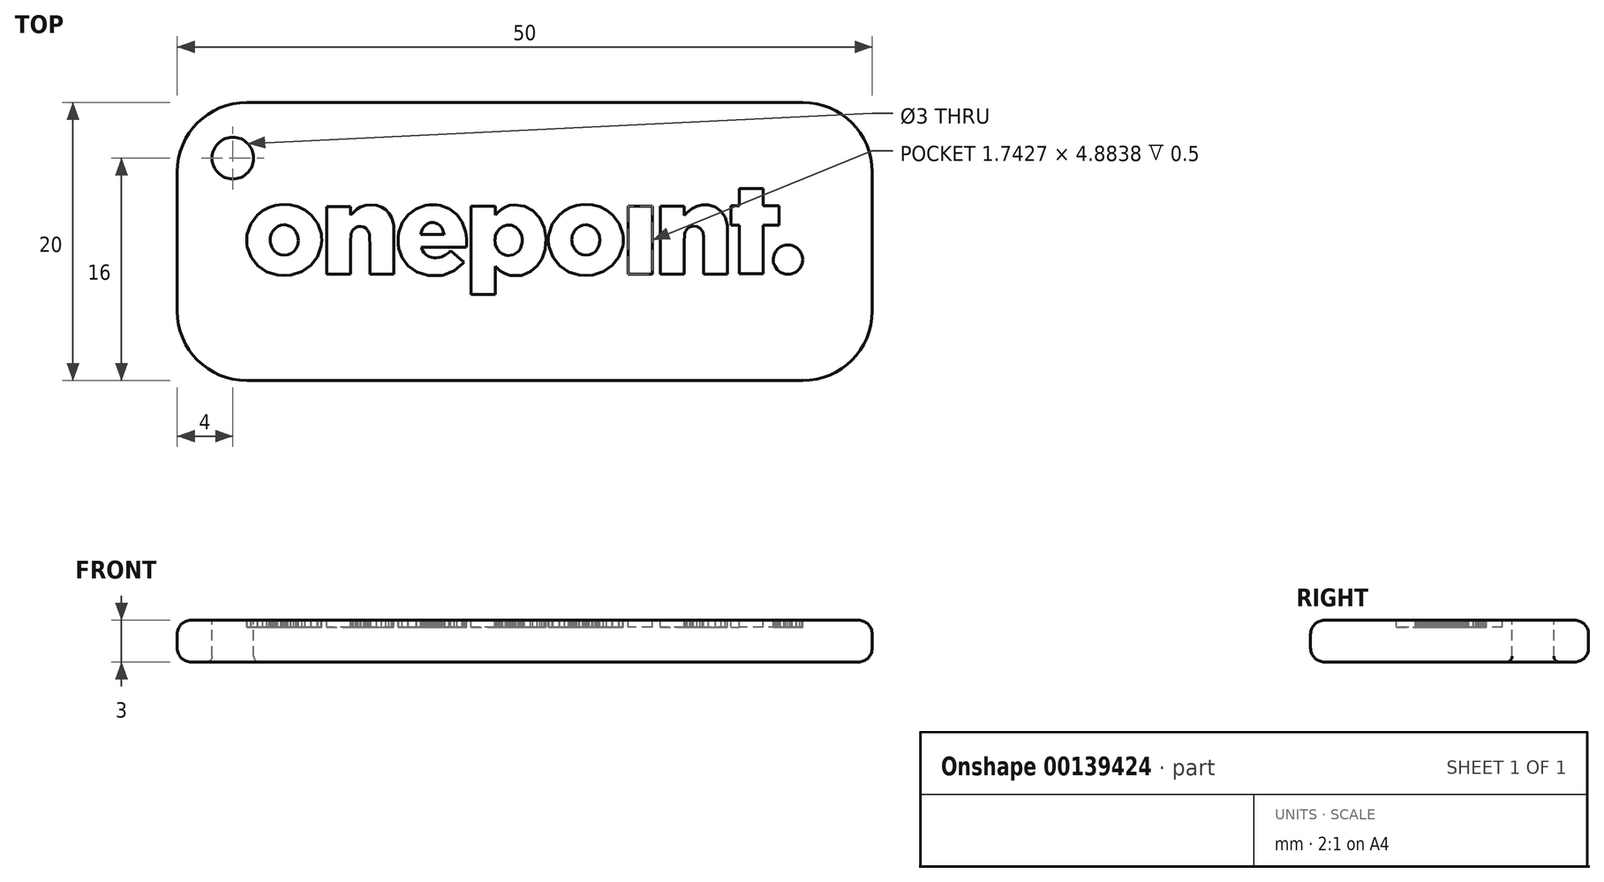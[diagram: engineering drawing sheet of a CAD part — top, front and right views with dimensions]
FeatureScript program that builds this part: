
annotation { "Feature Type Name" : "Feature", "Feature Type Description" : "" }
export const myFeature = defineFeature(function(context is Context, id is Id, definition is map)
    precondition{}
    {
        {
            var Q0;
            Q0=qCreatedBy(makeId("Top.planeOp"),FACE);
            var sketch = newSketch(context, id + "F0", { "sketchPlane" : qUnion([Q0])});
            skLineSegment(sketch, "E0.bottom", {"start": v(-25, 10) * mm, "end": v(25, 10) * mm});
            skLineSegment(sketch, "E0.top", {"start": v(-25, -10) * mm, "end": v(25, -10) * mm});
            skLineSegment(sketch, "E0.left", {"start": v(-25, 10) * mm, "end": v(-25, -10) * mm});
            skLineSegment(sketch, "E0.right", {"start": v(25, 10) * mm, "end": v(25, -10) * mm});
            skSolve(sketch);
        }
        {
            var Q0;
            Q0=qCreatedBy(makeId("Top.planeOp"),FACE);
            var sketch = newSketch(context, id + "F1", { "sketchPlane" : qUnion([Q0])});
            skLineSegment(sketch, "E1", {"start": v(-17.78, -2.42) * mm, "end": v(-18.55, -2.18) * mm});
            skLineSegment(sketch, "E2", {"start": v(-18.55, -2.18) * mm, "end": v(-19.2, -1.75) * mm});
            skLineSegment(sketch, "E3", {"start": v(-19.2, -1.75) * mm, "end": v(-19.67, -1.15) * mm});
            skLineSegment(sketch, "E4", {"start": v(-19.67, -1.15) * mm, "end": v(-19.95, -0.41) * mm});
            skLineSegment(sketch, "E5", {"start": v(-19.95, -0.41) * mm, "end": v(-19.99, -0.22) * mm});
            skLineSegment(sketch, "E6", {"start": v(-19.99, -0.22) * mm, "end": v(-20, 0.02) * mm});
            skLineSegment(sketch, "E7", {"start": v(-20, 0.02) * mm, "end": v(-20, 0.27) * mm});
            skLineSegment(sketch, "E8", {"start": v(-20, 0.27) * mm, "end": v(-19.98, 0.48) * mm});
            skLineSegment(sketch, "E9", {"start": v(-19.98, 0.48) * mm, "end": v(-19.72, 1.26) * mm});
            skLineSegment(sketch, "E10", {"start": v(-19.72, 1.26) * mm, "end": v(-19.22, 1.91) * mm});
            skLineSegment(sketch, "E11", {"start": v(-19.22, 1.91) * mm, "end": v(-18.84, 2.22) * mm});
            skLineSegment(sketch, "E12", {"start": v(-18.84, 2.22) * mm, "end": v(-18.41, 2.45) * mm});
            skLineSegment(sketch, "E13", {"start": v(-18.41, 2.45) * mm, "end": v(-17.94, 2.6) * mm});
            skLineSegment(sketch, "E14", {"start": v(-17.94, 2.6) * mm, "end": v(-17.43, 2.66) * mm});
            skLineSegment(sketch, "E15", {"start": v(-17.43, 2.66) * mm, "end": v(-16.85, 2.63) * mm});
            skLineSegment(sketch, "E16", {"start": v(-16.85, 2.63) * mm, "end": v(-16.3, 2.5) * mm});
            skLineSegment(sketch, "E17", {"start": v(-16.3, 2.5) * mm, "end": v(-15.8, 2.25) * mm});
            skLineSegment(sketch, "E18", {"start": v(-15.8, 2.25) * mm, "end": v(-15.37, 1.91) * mm});
            skLineSegment(sketch, "E19", {"start": v(-15.37, 1.91) * mm, "end": v(-14.89, 1.28) * mm});
            skLineSegment(sketch, "E20", {"start": v(-14.89, 1.28) * mm, "end": v(-14.63, 0.55) * mm});
            skLineSegment(sketch, "E21", {"start": v(-14.63, 0.55) * mm, "end": v(-14.61, 0.34) * mm});
            skLineSegment(sketch, "E22", {"start": v(-14.61, 0.34) * mm, "end": v(-14.6, 0.1) * mm});
            skLineSegment(sketch, "E23", {"start": v(-14.6, 0.1) * mm, "end": v(-14.62, -0.15) * mm});
            skLineSegment(sketch, "E24", {"start": v(-14.62, -0.15) * mm, "end": v(-14.65, -0.36) * mm});
            skLineSegment(sketch, "E25", {"start": v(-14.65, -0.36) * mm, "end": v(-14.92, -1.1) * mm});
            skLineSegment(sketch, "E26", {"start": v(-14.92, -1.1) * mm, "end": v(-15.39, -1.71) * mm});
            skLineSegment(sketch, "E27", {"start": v(-15.39, -1.71) * mm, "end": v(-16.03, -2.16) * mm});
            skLineSegment(sketch, "E28", {"start": v(-16.03, -2.16) * mm, "end": v(-16.8, -2.4) * mm});
            skLineSegment(sketch, "E29", {"start": v(-16.8, -2.4) * mm, "end": v(-17.3, -2.44) * mm});
            skLineSegment(sketch, "E30", {"start": v(-17.3, -2.44) * mm, "end": v(-17.78, -2.42) * mm});
            skLineSegment(sketch, "E31", {"start": v(-17.78, -2.42) * mm, "end": v(-17.78, -2.42) * mm});
            skLineSegment(sketch, "E32", {"start": v(-17.04, -0.95) * mm, "end": v(-16.81, -0.86) * mm});
            skLineSegment(sketch, "E33", {"start": v(-16.81, -0.86) * mm, "end": v(-16.62, -0.72) * mm});
            skLineSegment(sketch, "E34", {"start": v(-16.62, -0.72) * mm, "end": v(-16.47, -0.53) * mm});
            skLineSegment(sketch, "E35", {"start": v(-16.47, -0.53) * mm, "end": v(-16.35, -0.29) * mm});
            skLineSegment(sketch, "E36", {"start": v(-16.35, -0.29) * mm, "end": v(-16.3, 0.07) * mm});
            skLineSegment(sketch, "E37", {"start": v(-16.3, 0.07) * mm, "end": v(-16.33, 0.42) * mm});
            skLineSegment(sketch, "E38", {"start": v(-16.33, 0.42) * mm, "end": v(-16.46, 0.7) * mm});
            skLineSegment(sketch, "E39", {"start": v(-16.46, 0.7) * mm, "end": v(-16.63, 0.91) * mm});
            skLineSegment(sketch, "E40", {"start": v(-16.63, 0.91) * mm, "end": v(-16.86, 1.07) * mm});
            skLineSegment(sketch, "E41", {"start": v(-16.86, 1.07) * mm, "end": v(-17.12, 1.17) * mm});
            skLineSegment(sketch, "E42", {"start": v(-17.12, 1.17) * mm, "end": v(-17.23, 1.2) * mm});
            skLineSegment(sketch, "E43", {"start": v(-17.23, 1.2) * mm, "end": v(-17.32, 1.2) * mm});
            skLineSegment(sketch, "E44", {"start": v(-17.32, 1.2) * mm, "end": v(-17.54, 1.17) * mm});
            skLineSegment(sketch, "E45", {"start": v(-17.54, 1.17) * mm, "end": v(-17.76, 1.09) * mm});
            skLineSegment(sketch, "E46", {"start": v(-17.76, 1.09) * mm, "end": v(-17.94, 0.97) * mm});
            skLineSegment(sketch, "E47", {"start": v(-17.94, 0.97) * mm, "end": v(-18.1, 0.8) * mm});
            skLineSegment(sketch, "E48", {"start": v(-18.1, 0.8) * mm, "end": v(-18.2, 0.62) * mm});
            skLineSegment(sketch, "E49", {"start": v(-18.2, 0.62) * mm, "end": v(-18.28, 0.41) * mm});
            skLineSegment(sketch, "E50", {"start": v(-18.28, 0.41) * mm, "end": v(-18.3, 0.27) * mm});
            skLineSegment(sketch, "E51", {"start": v(-18.3, 0.27) * mm, "end": v(-18.32, 0.11) * mm});
            skLineSegment(sketch, "E52", {"start": v(-18.32, 0.11) * mm, "end": v(-18.3, -0.05) * mm});
            skLineSegment(sketch, "E53", {"start": v(-18.3, -0.05) * mm, "end": v(-18.28, -0.17) * mm});
            skLineSegment(sketch, "E54", {"start": v(-18.28, -0.17) * mm, "end": v(-18.18, -0.44) * mm});
            skLineSegment(sketch, "E55", {"start": v(-18.18, -0.44) * mm, "end": v(-18.01, -0.67) * mm});
            skLineSegment(sketch, "E56", {"start": v(-18.01, -0.67) * mm, "end": v(-17.8, -0.84) * mm});
            skLineSegment(sketch, "E57", {"start": v(-17.8, -0.84) * mm, "end": v(-17.55, -0.95) * mm});
            skLineSegment(sketch, "E58", {"start": v(-17.55, -0.95) * mm, "end": v(-17.3, -0.98) * mm});
            skLineSegment(sketch, "E59", {"start": v(-17.3, -0.98) * mm, "end": v(-17.04, -0.95) * mm});
            skLineSegment(sketch, "E60", {"start": v(-17.04, -0.95) * mm, "end": v(-17.04, -0.95) * mm});
            skLineSegment(sketch, "E61", {"start": v(-14.26, 0.08) * mm, "end": v(-14.26, 2.52) * mm});
            skLineSegment(sketch, "E62", {"start": v(-14.26, 2.52) * mm, "end": v(-12.53, 2.52) * mm});
            skLineSegment(sketch, "E63", {"start": v(-12.53, 2.52) * mm, "end": v(-12.53, 1.9) * mm});
            skLineSegment(sketch, "E64", {"start": v(-12.53, 1.9) * mm, "end": v(-12.34, 2.07) * mm});
            skLineSegment(sketch, "E65", {"start": v(-12.34, 2.07) * mm, "end": v(-12.09, 2.3) * mm});
            skLineSegment(sketch, "E66", {"start": v(-12.09, 2.3) * mm, "end": v(-11.81, 2.46) * mm});
            skLineSegment(sketch, "E67", {"start": v(-11.81, 2.46) * mm, "end": v(-11.46, 2.6) * mm});
            skLineSegment(sketch, "E68", {"start": v(-11.46, 2.6) * mm, "end": v(-11.07, 2.64) * mm});
            skLineSegment(sketch, "E69", {"start": v(-11.07, 2.64) * mm, "end": v(-10.67, 2.6) * mm});
            skLineSegment(sketch, "E70", {"start": v(-10.67, 2.6) * mm, "end": v(-10.3, 2.48) * mm});
            skLineSegment(sketch, "E71", {"start": v(-10.3, 2.48) * mm, "end": v(-10, 2.28) * mm});
            skLineSegment(sketch, "E72", {"start": v(-10, 2.28) * mm, "end": v(-9.75, 2.03) * mm});
            skLineSegment(sketch, "E73", {"start": v(-9.75, 2.03) * mm, "end": v(-9.57, 1.7) * mm});
            skLineSegment(sketch, "E74", {"start": v(-9.57, 1.7) * mm, "end": v(-9.45, 1.3) * mm});
            skLineSegment(sketch, "E75", {"start": v(-9.45, 1.3) * mm, "end": v(-9.44, 1.25) * mm});
            skLineSegment(sketch, "E76", {"start": v(-9.44, 1.25) * mm, "end": v(-9.43, 1.17) * mm});
            skLineSegment(sketch, "E77", {"start": v(-9.43, 1.17) * mm, "end": v(-9.43, 1.06) * mm});
            skLineSegment(sketch, "E78", {"start": v(-9.43, 1.06) * mm, "end": v(-9.42, 0.89) * mm});
            skLineSegment(sketch, "E79", {"start": v(-9.42, 0.89) * mm, "end": v(-9.42, 0.65) * mm});
            skLineSegment(sketch, "E80", {"start": v(-9.42, 0.65) * mm, "end": v(-9.41, 0.34) * mm});
            skLineSegment(sketch, "E81", {"start": v(-9.41, 0.34) * mm, "end": v(-9.41, -0.08) * mm});
            skLineSegment(sketch, "E82", {"start": v(-9.41, -0.08) * mm, "end": v(-9.4, -0.6) * mm});
            skLineSegment(sketch, "E83", {"start": v(-9.4, -0.6) * mm, "end": v(-9.4, -2.36) * mm});
            skLineSegment(sketch, "E84", {"start": v(-9.4, -2.36) * mm, "end": v(-11.14, -2.36) * mm});
            skLineSegment(sketch, "E85", {"start": v(-11.14, -2.36) * mm, "end": v(-11.14, -0.94) * mm});
            skLineSegment(sketch, "E86", {"start": v(-11.14, -0.94) * mm, "end": v(-11.14, -0.47) * mm});
            skLineSegment(sketch, "E87", {"start": v(-11.14, -0.47) * mm, "end": v(-11.15, -0.12) * mm});
            skLineSegment(sketch, "E88", {"start": v(-11.15, -0.12) * mm, "end": v(-11.15, 0.14) * mm});
            skLineSegment(sketch, "E89", {"start": v(-11.15, 0.14) * mm, "end": v(-11.15, 0.32) * mm});
            skLineSegment(sketch, "E90", {"start": v(-11.15, 0.32) * mm, "end": v(-11.16, 0.44) * mm});
            skLineSegment(sketch, "E91", {"start": v(-11.16, 0.44) * mm, "end": v(-11.16, 0.52) * mm});
            skLineSegment(sketch, "E92", {"start": v(-11.16, 0.52) * mm, "end": v(-11.17, 0.57) * mm});
            skLineSegment(sketch, "E93", {"start": v(-11.17, 0.57) * mm, "end": v(-11.19, 0.6) * mm});
            skLineSegment(sketch, "E94", {"start": v(-11.19, 0.6) * mm, "end": v(-11.28, 0.8) * mm});
            skLineSegment(sketch, "E95", {"start": v(-11.28, 0.8) * mm, "end": v(-11.4, 0.95) * mm});
            skLineSegment(sketch, "E96", {"start": v(-11.4, 0.95) * mm, "end": v(-11.56, 1.05) * mm});
            skLineSegment(sketch, "E97", {"start": v(-11.56, 1.05) * mm, "end": v(-11.76, 1.09) * mm});
            skLineSegment(sketch, "E98", {"start": v(-11.76, 1.09) * mm, "end": v(-11.99, 1.08) * mm});
            skLineSegment(sketch, "E99", {"start": v(-11.99, 1.08) * mm, "end": v(-12.2, 0.99) * mm});
            skLineSegment(sketch, "E100", {"start": v(-12.2, 0.99) * mm, "end": v(-12.36, 0.84) * mm});
            skLineSegment(sketch, "E101", {"start": v(-12.36, 0.84) * mm, "end": v(-12.48, 0.63) * mm});
            skLineSegment(sketch, "E102", {"start": v(-12.48, 0.63) * mm, "end": v(-12.5, 0.6) * mm});
            skLineSegment(sketch, "E103", {"start": v(-12.5, 0.6) * mm, "end": v(-12.5, 0.55) * mm});
            skLineSegment(sketch, "E104", {"start": v(-12.5, 0.55) * mm, "end": v(-12.5, 0.47) * mm});
            skLineSegment(sketch, "E105", {"start": v(-12.5, 0.47) * mm, "end": v(-12.51, 0.35) * mm});
            skLineSegment(sketch, "E106", {"start": v(-12.51, 0.35) * mm, "end": v(-12.52, 0.17) * mm});
            skLineSegment(sketch, "E107", {"start": v(-12.52, 0.17) * mm, "end": v(-12.52, -0.1) * mm});
            skLineSegment(sketch, "E108", {"start": v(-12.52, -0.1) * mm, "end": v(-12.52, -0.45) * mm});
            skLineSegment(sketch, "E109", {"start": v(-12.52, -0.45) * mm, "end": v(-12.53, -0.92) * mm});
            skLineSegment(sketch, "E110", {"start": v(-12.53, -0.92) * mm, "end": v(-12.53, -2.36) * mm});
            skLineSegment(sketch, "E111", {"start": v(-12.53, -2.36) * mm, "end": v(-14.26, -2.36) * mm});
            skLineSegment(sketch, "E112", {"start": v(-14.26, -2.36) * mm, "end": v(-14.26, 0.08) * mm});
            skLineSegment(sketch, "E113", {"start": v(-14.26, 0.08) * mm, "end": v(-14.26, 0.08) * mm});
            skLineSegment(sketch, "E114", {"start": v(-6.94, -2.44) * mm, "end": v(-7.76, -2.2) * mm});
            skLineSegment(sketch, "E115", {"start": v(-7.76, -2.2) * mm, "end": v(-8.4, -1.73) * mm});
            skLineSegment(sketch, "E116", {"start": v(-8.4, -1.73) * mm, "end": v(-8.83, -1.18) * mm});
            skLineSegment(sketch, "E117", {"start": v(-8.83, -1.18) * mm, "end": v(-9.06, -0.5) * mm});
            skLineSegment(sketch, "E118", {"start": v(-9.06, -0.5) * mm, "end": v(-9.08, -0.4) * mm});
            skLineSegment(sketch, "E119", {"start": v(-9.08, -0.4) * mm, "end": v(-9.1, -0.28) * mm});
            skLineSegment(sketch, "E120", {"start": v(-9.1, -0.28) * mm, "end": v(-9.1, -0.13) * mm});
            skLineSegment(sketch, "E121", {"start": v(-9.1, -0.13) * mm, "end": v(-9.1, 0.07) * mm});
            skLineSegment(sketch, "E122", {"start": v(-9.1, 0.07) * mm, "end": v(-9.1, 0.28) * mm});
            skLineSegment(sketch, "E123", {"start": v(-9.1, 0.28) * mm, "end": v(-9.1, 0.42) * mm});
            skLineSegment(sketch, "E124", {"start": v(-9.1, 0.42) * mm, "end": v(-9.08, 0.53) * mm});
            skLineSegment(sketch, "E125", {"start": v(-9.08, 0.53) * mm, "end": v(-9.06, 0.64) * mm});
            skLineSegment(sketch, "E126", {"start": v(-9.06, 0.64) * mm, "end": v(-8.8, 1.35) * mm});
            skLineSegment(sketch, "E127", {"start": v(-8.8, 1.35) * mm, "end": v(-8.38, 1.94) * mm});
            skLineSegment(sketch, "E128", {"start": v(-8.38, 1.94) * mm, "end": v(-7.81, 2.36) * mm});
            skLineSegment(sketch, "E129", {"start": v(-7.81, 2.36) * mm, "end": v(-7.13, 2.6) * mm});
            skLineSegment(sketch, "E130", {"start": v(-7.13, 2.6) * mm, "end": v(-6.9, 2.63) * mm});
            skLineSegment(sketch, "E131", {"start": v(-6.9, 2.63) * mm, "end": v(-6.6, 2.64) * mm});
            skLineSegment(sketch, "E132", {"start": v(-6.6, 2.64) * mm, "end": v(-6.32, 2.62) * mm});
            skLineSegment(sketch, "E133", {"start": v(-6.32, 2.62) * mm, "end": v(-6.08, 2.6) * mm});
            skLineSegment(sketch, "E134", {"start": v(-6.08, 2.6) * mm, "end": v(-5.41, 2.36) * mm});
            skLineSegment(sketch, "E135", {"start": v(-5.41, 2.36) * mm, "end": v(-4.88, 1.95) * mm});
            skLineSegment(sketch, "E136", {"start": v(-4.88, 1.95) * mm, "end": v(-4.5, 1.39) * mm});
            skLineSegment(sketch, "E137", {"start": v(-4.5, 1.39) * mm, "end": v(-4.25, 0.68) * mm});
            skLineSegment(sketch, "E138", {"start": v(-4.25, 0.68) * mm, "end": v(-4.22, 0.46) * mm});
            skLineSegment(sketch, "E139", {"start": v(-4.22, 0.46) * mm, "end": v(-4.2, 0.2) * mm});
            skLineSegment(sketch, "E140", {"start": v(-4.2, 0.2) * mm, "end": v(-4.18, -0.06) * mm});
            skLineSegment(sketch, "E141", {"start": v(-4.18, -0.06) * mm, "end": v(-4.18, -0.25) * mm});
            skLineSegment(sketch, "E142", {"start": v(-4.18, -0.25) * mm, "end": v(-4.2, -0.4) * mm});
            skLineSegment(sketch, "E143", {"start": v(-4.2, -0.4) * mm, "end": v(-7.45, -0.4) * mm});
            skLineSegment(sketch, "E144", {"start": v(-7.45, -0.4) * mm, "end": v(-7.43, -0.45) * mm});
            skLineSegment(sketch, "E145", {"start": v(-7.43, -0.45) * mm, "end": v(-7.41, -0.52) * mm});
            skLineSegment(sketch, "E146", {"start": v(-7.41, -0.52) * mm, "end": v(-7.36, -0.62) * mm});
            skLineSegment(sketch, "E147", {"start": v(-7.36, -0.62) * mm, "end": v(-7.25, -0.8) * mm});
            skLineSegment(sketch, "E148", {"start": v(-7.25, -0.8) * mm, "end": v(-7.1, -0.96) * mm});
            skLineSegment(sketch, "E149", {"start": v(-7.1, -0.96) * mm, "end": v(-6.91, -1.07) * mm});
            skLineSegment(sketch, "E150", {"start": v(-6.91, -1.07) * mm, "end": v(-6.7, -1.15) * mm});
            skLineSegment(sketch, "E151", {"start": v(-6.7, -1.15) * mm, "end": v(-6.53, -1.17) * mm});
            skLineSegment(sketch, "E152", {"start": v(-6.53, -1.17) * mm, "end": v(-6.33, -1.17) * mm});
            skLineSegment(sketch, "E153", {"start": v(-6.33, -1.17) * mm, "end": v(-6.14, -1.15) * mm});
            skLineSegment(sketch, "E154", {"start": v(-6.14, -1.15) * mm, "end": v(-5.98, -1.11) * mm});
            skLineSegment(sketch, "E155", {"start": v(-5.98, -1.11) * mm, "end": v(-5.72, -0.98) * mm});
            skLineSegment(sketch, "E156", {"start": v(-5.72, -0.98) * mm, "end": v(-5.46, -0.8) * mm});
            skLineSegment(sketch, "E157", {"start": v(-5.46, -0.8) * mm, "end": v(-5.32, -0.68) * mm});
            skLineSegment(sketch, "E158", {"start": v(-5.32, -0.68) * mm, "end": v(-4.84, -1.08) * mm});
            skLineSegment(sketch, "E159", {"start": v(-4.84, -1.08) * mm, "end": v(-4.36, -1.48) * mm});
            skLineSegment(sketch, "E160", {"start": v(-4.36, -1.48) * mm, "end": v(-4.45, -1.58) * mm});
            skLineSegment(sketch, "E161", {"start": v(-4.45, -1.58) * mm, "end": v(-5.07, -2.1) * mm});
            skLineSegment(sketch, "E162", {"start": v(-5.07, -2.1) * mm, "end": v(-5.83, -2.4) * mm});
            skLineSegment(sketch, "E163", {"start": v(-5.83, -2.4) * mm, "end": v(-5.95, -2.43) * mm});
            skLineSegment(sketch, "E164", {"start": v(-5.95, -2.43) * mm, "end": v(-6.06, -2.44) * mm});
            skLineSegment(sketch, "E165", {"start": v(-6.06, -2.44) * mm, "end": v(-6.22, -2.45) * mm});
            skLineSegment(sketch, "E166", {"start": v(-6.22, -2.45) * mm, "end": v(-6.44, -2.45) * mm});
            skLineSegment(sketch, "E167", {"start": v(-6.44, -2.45) * mm, "end": v(-6.6, -2.46) * mm});
            skLineSegment(sketch, "E168", {"start": v(-6.6, -2.46) * mm, "end": v(-6.75, -2.46) * mm});
            skLineSegment(sketch, "E169", {"start": v(-6.75, -2.46) * mm, "end": v(-6.87, -2.45) * mm});
            skLineSegment(sketch, "E170", {"start": v(-6.87, -2.45) * mm, "end": v(-6.94, -2.44) * mm});
            skLineSegment(sketch, "E171", {"start": v(-6.94, -2.44) * mm, "end": v(-6.94, -2.44) * mm});
            skLineSegment(sketch, "E172", {"start": v(-5.8, 0.53) * mm, "end": v(-5.82, 0.6) * mm});
            skLineSegment(sketch, "E173", {"start": v(-5.82, 0.6) * mm, "end": v(-5.85, 0.7) * mm});
            skLineSegment(sketch, "E174", {"start": v(-5.85, 0.7) * mm, "end": v(-5.89, 0.82) * mm});
            skLineSegment(sketch, "E175", {"start": v(-5.89, 0.82) * mm, "end": v(-5.93, 0.92) * mm});
            skLineSegment(sketch, "E176", {"start": v(-5.93, 0.92) * mm, "end": v(-6.08, 1.13) * mm});
            skLineSegment(sketch, "E177", {"start": v(-6.08, 1.13) * mm, "end": v(-6.28, 1.28) * mm});
            skLineSegment(sketch, "E178", {"start": v(-6.28, 1.28) * mm, "end": v(-6.52, 1.35) * mm});
            skLineSegment(sketch, "E179", {"start": v(-6.52, 1.35) * mm, "end": v(-6.77, 1.35) * mm});
            skLineSegment(sketch, "E180", {"start": v(-6.77, 1.35) * mm, "end": v(-7, 1.27) * mm});
            skLineSegment(sketch, "E181", {"start": v(-7, 1.27) * mm, "end": v(-7.2, 1.12) * mm});
            skLineSegment(sketch, "E182", {"start": v(-7.2, 1.12) * mm, "end": v(-7.34, 0.91) * mm});
            skLineSegment(sketch, "E183", {"start": v(-7.34, 0.91) * mm, "end": v(-7.45, 0.64) * mm});
            skLineSegment(sketch, "E184", {"start": v(-7.45, 0.64) * mm, "end": v(-7.48, 0.5) * mm});
            skLineSegment(sketch, "E185", {"start": v(-7.48, 0.5) * mm, "end": v(-6.64, 0.5) * mm});
            skLineSegment(sketch, "E186", {"start": v(-6.64, 0.5) * mm, "end": v(-6.4, 0.5) * mm});
            skLineSegment(sketch, "E187", {"start": v(-6.4, 0.5) * mm, "end": v(-6.2, 0.5) * mm});
            skLineSegment(sketch, "E188", {"start": v(-6.2, 0.5) * mm, "end": v(-6.05, 0.5) * mm});
            skLineSegment(sketch, "E189", {"start": v(-6.05, 0.5) * mm, "end": v(-5.94, 0.5) * mm});
            skLineSegment(sketch, "E190", {"start": v(-5.94, 0.5) * mm, "end": v(-5.87, 0.51) * mm});
            skLineSegment(sketch, "E191", {"start": v(-5.87, 0.51) * mm, "end": v(-5.83, 0.51) * mm});
            skLineSegment(sketch, "E192", {"start": v(-5.83, 0.51) * mm, "end": v(-5.81, 0.52) * mm});
            skLineSegment(sketch, "E193", {"start": v(-5.81, 0.52) * mm, "end": v(-5.8, 0.53) * mm});
            skLineSegment(sketch, "E194", {"start": v(-5.8, 0.53) * mm, "end": v(-5.8, 0.53) * mm});
            skLineSegment(sketch, "E195", {"start": v(-3.85, -0.63) * mm, "end": v(-3.85, 2.53) * mm});
            skLineSegment(sketch, "E196", {"start": v(-3.85, 2.53) * mm, "end": v(-2.12, 2.53) * mm});
            skLineSegment(sketch, "E197", {"start": v(-2.12, 2.53) * mm, "end": v(-2.12, 1.9) * mm});
            skLineSegment(sketch, "E198", {"start": v(-2.12, 1.9) * mm, "end": v(-1.95, 2.07) * mm});
            skLineSegment(sketch, "E199", {"start": v(-1.95, 2.07) * mm, "end": v(-1.68, 2.31) * mm});
            skLineSegment(sketch, "E200", {"start": v(-1.68, 2.31) * mm, "end": v(-1.4, 2.48) * mm});
            skLineSegment(sketch, "E201", {"start": v(-1.4, 2.48) * mm, "end": v(-1.09, 2.6) * mm});
            skLineSegment(sketch, "E202", {"start": v(-1.09, 2.6) * mm, "end": v(-0.74, 2.64) * mm});
            skLineSegment(sketch, "E203", {"start": v(-0.74, 2.64) * mm, "end": v(-0.03, 2.55) * mm});
            skLineSegment(sketch, "E204", {"start": v(-0.03, 2.55) * mm, "end": v(0.6, 2.22) * mm});
            skLineSegment(sketch, "E205", {"start": v(0.6, 2.22) * mm, "end": v(1.08, 1.7) * mm});
            skLineSegment(sketch, "E206", {"start": v(1.08, 1.7) * mm, "end": v(1.4, 1) * mm});
            skLineSegment(sketch, "E207", {"start": v(1.4, 1) * mm, "end": v(1.52, 0.22) * mm});
            skLineSegment(sketch, "E208", {"start": v(1.52, 0.22) * mm, "end": v(1.46, -0.58) * mm});
            skLineSegment(sketch, "E209", {"start": v(1.46, -0.58) * mm, "end": v(1.25, -1.23) * mm});
            skLineSegment(sketch, "E210", {"start": v(1.25, -1.23) * mm, "end": v(0.9, -1.76) * mm});
            skLineSegment(sketch, "E211", {"start": v(0.9, -1.76) * mm, "end": v(0.43, -2.16) * mm});
            skLineSegment(sketch, "E212", {"start": v(0.43, -2.16) * mm, "end": v(-0.13, -2.4) * mm});
            skLineSegment(sketch, "E213", {"start": v(-0.13, -2.4) * mm, "end": v(-0.25, -2.43) * mm});
            skLineSegment(sketch, "E214", {"start": v(-0.25, -2.43) * mm, "end": v(-0.35, -2.45) * mm});
            skLineSegment(sketch, "E215", {"start": v(-0.35, -2.45) * mm, "end": v(-0.47, -2.45) * mm});
            skLineSegment(sketch, "E216", {"start": v(-0.47, -2.45) * mm, "end": v(-0.64, -2.45) * mm});
            skLineSegment(sketch, "E217", {"start": v(-0.64, -2.45) * mm, "end": v(-0.81, -2.45) * mm});
            skLineSegment(sketch, "E218", {"start": v(-0.81, -2.45) * mm, "end": v(-0.94, -2.45) * mm});
            skLineSegment(sketch, "E219", {"start": v(-0.94, -2.45) * mm, "end": v(-1.04, -2.43) * mm});
            skLineSegment(sketch, "E220", {"start": v(-1.04, -2.43) * mm, "end": v(-1.14, -2.4) * mm});
            skLineSegment(sketch, "E221", {"start": v(-1.14, -2.4) * mm, "end": v(-1.37, -2.33) * mm});
            skLineSegment(sketch, "E222", {"start": v(-1.37, -2.33) * mm, "end": v(-1.58, -2.23) * mm});
            skLineSegment(sketch, "E223", {"start": v(-1.58, -2.23) * mm, "end": v(-1.78, -2.09) * mm});
            skLineSegment(sketch, "E224", {"start": v(-1.78, -2.09) * mm, "end": v(-1.98, -1.91) * mm});
            skLineSegment(sketch, "E225", {"start": v(-1.98, -1.91) * mm, "end": v(-2.12, -1.79) * mm});
            skLineSegment(sketch, "E226", {"start": v(-2.12, -1.79) * mm, "end": v(-2.12, -3.8) * mm});
            skLineSegment(sketch, "E227", {"start": v(-2.12, -3.8) * mm, "end": v(-3.85, -3.8) * mm});
            skLineSegment(sketch, "E228", {"start": v(-3.85, -3.8) * mm, "end": v(-3.85, -0.63) * mm});
            skLineSegment(sketch, "E229", {"start": v(-3.85, -0.63) * mm, "end": v(-3.85, -0.63) * mm});
            skLineSegment(sketch, "E230", {"start": v(-1, -1) * mm, "end": v(-0.8, -0.94) * mm});
            skLineSegment(sketch, "E231", {"start": v(-0.8, -0.94) * mm, "end": v(-0.61, -0.83) * mm});
            skLineSegment(sketch, "E232", {"start": v(-0.61, -0.83) * mm, "end": v(-0.44, -0.68) * mm});
            skLineSegment(sketch, "E233", {"start": v(-0.44, -0.68) * mm, "end": v(-0.32, -0.5) * mm});
            skLineSegment(sketch, "E234", {"start": v(-0.32, -0.5) * mm, "end": v(-0.23, -0.3) * mm});
            skLineSegment(sketch, "E235", {"start": v(-0.23, -0.3) * mm, "end": v(-0.19, -0.06) * mm});
            skLineSegment(sketch, "E236", {"start": v(-0.19, -0.06) * mm, "end": v(-0.18, 0.18) * mm});
            skLineSegment(sketch, "E237", {"start": v(-0.18, 0.18) * mm, "end": v(-0.22, 0.41) * mm});
            skLineSegment(sketch, "E238", {"start": v(-0.22, 0.41) * mm, "end": v(-0.38, 0.76) * mm});
            skLineSegment(sketch, "E239", {"start": v(-0.38, 0.76) * mm, "end": v(-0.63, 1.02) * mm});
            skLineSegment(sketch, "E240", {"start": v(-0.63, 1.02) * mm, "end": v(-0.94, 1.16) * mm});
            skLineSegment(sketch, "E241", {"start": v(-0.94, 1.16) * mm, "end": v(-1.3, 1.18) * mm});
            skLineSegment(sketch, "E242", {"start": v(-1.3, 1.18) * mm, "end": v(-1.57, 1.1) * mm});
            skLineSegment(sketch, "E243", {"start": v(-1.57, 1.1) * mm, "end": v(-1.8, 0.92) * mm});
            skLineSegment(sketch, "E244", {"start": v(-1.8, 0.92) * mm, "end": v(-1.99, 0.69) * mm});
            skLineSegment(sketch, "E245", {"start": v(-1.99, 0.69) * mm, "end": v(-2.1, 0.4) * mm});
            skLineSegment(sketch, "E246", {"start": v(-2.1, 0.4) * mm, "end": v(-2.13, 0.26) * mm});
            skLineSegment(sketch, "E247", {"start": v(-2.13, 0.26) * mm, "end": v(-2.14, 0.1) * mm});
            skLineSegment(sketch, "E248", {"start": v(-2.14, 0.1) * mm, "end": v(-2.13, -0.08) * mm});
            skLineSegment(sketch, "E249", {"start": v(-2.13, -0.08) * mm, "end": v(-2.1, -0.22) * mm});
            skLineSegment(sketch, "E250", {"start": v(-2.1, -0.22) * mm, "end": v(-2, -0.5) * mm});
            skLineSegment(sketch, "E251", {"start": v(-2, -0.5) * mm, "end": v(-1.83, -0.73) * mm});
            skLineSegment(sketch, "E252", {"start": v(-1.83, -0.73) * mm, "end": v(-1.61, -0.9) * mm});
            skLineSegment(sketch, "E253", {"start": v(-1.61, -0.9) * mm, "end": v(-1.36, -1) * mm});
            skLineSegment(sketch, "E254", {"start": v(-1.36, -1) * mm, "end": v(-1.19, -1.01) * mm});
            skLineSegment(sketch, "E255", {"start": v(-1.19, -1.01) * mm, "end": v(-1, -1) * mm});
            skLineSegment(sketch, "E256", {"start": v(7.43, 0.1) * mm, "end": v(7.43, 2.53) * mm});
            skLineSegment(sketch, "E257", {"start": v(7.43, 2.53) * mm, "end": v(9.18, 2.53) * mm});
            skLineSegment(sketch, "E258", {"start": v(9.18, 2.53) * mm, "end": v(9.18, -2.35) * mm});
            skLineSegment(sketch, "E259", {"start": v(9.18, -2.35) * mm, "end": v(7.43, -2.35) * mm});
            skLineSegment(sketch, "E260", {"start": v(7.43, -2.35) * mm, "end": v(7.43, 0.1) * mm});
            skLineSegment(sketch, "E261", {"start": v(3.93, -2.42) * mm, "end": v(3.15, -2.18) * mm});
            skLineSegment(sketch, "E262", {"start": v(3.15, -2.18) * mm, "end": v(2.5, -1.75) * mm});
            skLineSegment(sketch, "E263", {"start": v(2.5, -1.75) * mm, "end": v(2.03, -1.15) * mm});
            skLineSegment(sketch, "E264", {"start": v(2.03, -1.15) * mm, "end": v(1.75, -0.41) * mm});
            skLineSegment(sketch, "E265", {"start": v(1.75, -0.41) * mm, "end": v(1.72, -0.22) * mm});
            skLineSegment(sketch, "E266", {"start": v(1.72, -0.22) * mm, "end": v(1.7, 0.02) * mm});
            skLineSegment(sketch, "E267", {"start": v(1.7, 0.02) * mm, "end": v(1.7, 0.27) * mm});
            skLineSegment(sketch, "E268", {"start": v(1.7, 0.27) * mm, "end": v(1.73, 0.48) * mm});
            skLineSegment(sketch, "E269", {"start": v(1.73, 0.48) * mm, "end": v(1.98, 1.26) * mm});
            skLineSegment(sketch, "E270", {"start": v(1.98, 1.26) * mm, "end": v(2.48, 1.91) * mm});
            skLineSegment(sketch, "E271", {"start": v(2.48, 1.91) * mm, "end": v(2.86, 2.22) * mm});
            skLineSegment(sketch, "E272", {"start": v(2.86, 2.22) * mm, "end": v(3.3, 2.45) * mm});
            skLineSegment(sketch, "E273", {"start": v(3.3, 2.45) * mm, "end": v(3.76, 2.6) * mm});
            skLineSegment(sketch, "E274", {"start": v(3.76, 2.6) * mm, "end": v(4.27, 2.66) * mm});
            skLineSegment(sketch, "E275", {"start": v(4.27, 2.66) * mm, "end": v(4.86, 2.63) * mm});
            skLineSegment(sketch, "E276", {"start": v(4.86, 2.63) * mm, "end": v(5.4, 2.5) * mm});
            skLineSegment(sketch, "E277", {"start": v(5.4, 2.5) * mm, "end": v(5.9, 2.25) * mm});
            skLineSegment(sketch, "E278", {"start": v(5.9, 2.25) * mm, "end": v(6.33, 1.91) * mm});
            skLineSegment(sketch, "E279", {"start": v(6.33, 1.91) * mm, "end": v(6.81, 1.28) * mm});
            skLineSegment(sketch, "E280", {"start": v(6.81, 1.28) * mm, "end": v(7.07, 0.55) * mm});
            skLineSegment(sketch, "E281", {"start": v(7.07, 0.55) * mm, "end": v(7.1, 0.34) * mm});
            skLineSegment(sketch, "E282", {"start": v(7.1, 0.34) * mm, "end": v(7.1, 0.1) * mm});
            skLineSegment(sketch, "E283", {"start": v(7.1, 0.1) * mm, "end": v(7.08, -0.15) * mm});
            skLineSegment(sketch, "E284", {"start": v(7.08, -0.15) * mm, "end": v(7.06, -0.36) * mm});
            skLineSegment(sketch, "E285", {"start": v(7.06, -0.36) * mm, "end": v(6.79, -1.1) * mm});
            skLineSegment(sketch, "E286", {"start": v(6.79, -1.1) * mm, "end": v(6.31, -1.71) * mm});
            skLineSegment(sketch, "E287", {"start": v(6.31, -1.71) * mm, "end": v(5.67, -2.16) * mm});
            skLineSegment(sketch, "E288", {"start": v(5.67, -2.16) * mm, "end": v(4.9, -2.4) * mm});
            skLineSegment(sketch, "E289", {"start": v(4.9, -2.4) * mm, "end": v(4.4, -2.44) * mm});
            skLineSegment(sketch, "E290", {"start": v(4.4, -2.44) * mm, "end": v(3.93, -2.42) * mm});
            skLineSegment(sketch, "E291", {"start": v(4.66, -0.95) * mm, "end": v(4.9, -0.86) * mm});
            skLineSegment(sketch, "E292", {"start": v(4.9, -0.86) * mm, "end": v(5.08, -0.72) * mm});
            skLineSegment(sketch, "E293", {"start": v(5.08, -0.72) * mm, "end": v(5.23, -0.53) * mm});
            skLineSegment(sketch, "E294", {"start": v(5.23, -0.53) * mm, "end": v(5.35, -0.29) * mm});
            skLineSegment(sketch, "E295", {"start": v(5.35, -0.29) * mm, "end": v(5.41, 0.07) * mm});
            skLineSegment(sketch, "E296", {"start": v(5.41, 0.07) * mm, "end": v(5.37, 0.42) * mm});
            skLineSegment(sketch, "E297", {"start": v(5.37, 0.42) * mm, "end": v(5.25, 0.7) * mm});
            skLineSegment(sketch, "E298", {"start": v(5.25, 0.7) * mm, "end": v(5.07, 0.91) * mm});
            skLineSegment(sketch, "E299", {"start": v(5.07, 0.91) * mm, "end": v(4.84, 1.07) * mm});
            skLineSegment(sketch, "E300", {"start": v(4.84, 1.07) * mm, "end": v(4.58, 1.17) * mm});
            skLineSegment(sketch, "E301", {"start": v(4.58, 1.17) * mm, "end": v(4.47, 1.2) * mm});
            skLineSegment(sketch, "E302", {"start": v(4.47, 1.2) * mm, "end": v(4.38, 1.2) * mm});
            skLineSegment(sketch, "E303", {"start": v(4.38, 1.2) * mm, "end": v(4.17, 1.17) * mm});
            skLineSegment(sketch, "E304", {"start": v(4.17, 1.17) * mm, "end": v(3.94, 1.09) * mm});
            skLineSegment(sketch, "E305", {"start": v(3.94, 1.09) * mm, "end": v(3.76, 0.97) * mm});
            skLineSegment(sketch, "E306", {"start": v(3.76, 0.97) * mm, "end": v(3.61, 0.8) * mm});
            skLineSegment(sketch, "E307", {"start": v(3.61, 0.8) * mm, "end": v(3.5, 0.62) * mm});
            skLineSegment(sketch, "E308", {"start": v(3.5, 0.62) * mm, "end": v(3.42, 0.41) * mm});
            skLineSegment(sketch, "E309", {"start": v(3.42, 0.41) * mm, "end": v(3.4, 0.27) * mm});
            skLineSegment(sketch, "E310", {"start": v(3.4, 0.27) * mm, "end": v(3.39, 0.11) * mm});
            skLineSegment(sketch, "E311", {"start": v(3.39, 0.11) * mm, "end": v(3.4, -0.05) * mm});
            skLineSegment(sketch, "E312", {"start": v(3.4, -0.05) * mm, "end": v(3.42, -0.17) * mm});
            skLineSegment(sketch, "E313", {"start": v(3.42, -0.17) * mm, "end": v(3.52, -0.44) * mm});
            skLineSegment(sketch, "E314", {"start": v(3.52, -0.44) * mm, "end": v(3.69, -0.67) * mm});
            skLineSegment(sketch, "E315", {"start": v(3.69, -0.67) * mm, "end": v(3.9, -0.84) * mm});
            skLineSegment(sketch, "E316", {"start": v(3.9, -0.84) * mm, "end": v(4.16, -0.95) * mm});
            skLineSegment(sketch, "E317", {"start": v(4.16, -0.95) * mm, "end": v(4.4, -0.98) * mm});
            skLineSegment(sketch, "E318", {"start": v(4.4, -0.98) * mm, "end": v(4.66, -0.95) * mm});
            skLineSegment(sketch, "E319", {"start": v(4.66, -0.95) * mm, "end": v(4.66, -0.95) * mm});
            skLineSegment(sketch, "E320", {"start": v(9.75, 0.1) * mm, "end": v(9.75, 2.53) * mm});
            skLineSegment(sketch, "E321", {"start": v(9.75, 2.53) * mm, "end": v(11.48, 2.53) * mm});
            skLineSegment(sketch, "E322", {"start": v(11.48, 2.53) * mm, "end": v(11.48, 1.88) * mm});
            skLineSegment(sketch, "E323", {"start": v(11.48, 1.88) * mm, "end": v(11.66, 2.06) * mm});
            skLineSegment(sketch, "E324", {"start": v(11.66, 2.06) * mm, "end": v(12.01, 2.36) * mm});
            skLineSegment(sketch, "E325", {"start": v(12.01, 2.36) * mm, "end": v(12.38, 2.56) * mm});
            skLineSegment(sketch, "E326", {"start": v(12.38, 2.56) * mm, "end": v(12.79, 2.64) * mm});
            skLineSegment(sketch, "E327", {"start": v(12.79, 2.64) * mm, "end": v(13.22, 2.63) * mm});
            skLineSegment(sketch, "E328", {"start": v(13.22, 2.63) * mm, "end": v(13.74, 2.47) * mm});
            skLineSegment(sketch, "E329", {"start": v(13.74, 2.47) * mm, "end": v(14.15, 2.17) * mm});
            skLineSegment(sketch, "E330", {"start": v(14.15, 2.17) * mm, "end": v(14.43, 1.74) * mm});
            skLineSegment(sketch, "E331", {"start": v(14.43, 1.74) * mm, "end": v(14.58, 1.18) * mm});
            skLineSegment(sketch, "E332", {"start": v(14.58, 1.18) * mm, "end": v(14.59, 1) * mm});
            skLineSegment(sketch, "E333", {"start": v(14.59, 1) * mm, "end": v(14.6, 0.6) * mm});
            skLineSegment(sketch, "E334", {"start": v(14.6, 0.6) * mm, "end": v(14.6, 0.04) * mm});
            skLineSegment(sketch, "E335", {"start": v(14.6, 0.04) * mm, "end": v(14.6, -0.65) * mm});
            skLineSegment(sketch, "E336", {"start": v(14.6, -0.65) * mm, "end": v(14.6, -2.35) * mm});
            skLineSegment(sketch, "E337", {"start": v(14.6, -2.35) * mm, "end": v(12.87, -2.35) * mm});
            skLineSegment(sketch, "E338", {"start": v(12.87, -2.35) * mm, "end": v(12.87, -0.96) * mm});
            skLineSegment(sketch, "E339", {"start": v(12.87, -0.96) * mm, "end": v(12.87, -0.46) * mm});
            skLineSegment(sketch, "E340", {"start": v(12.87, -0.46) * mm, "end": v(12.87, -0.08) * mm});
            skLineSegment(sketch, "E341", {"start": v(12.87, -0.08) * mm, "end": v(12.86, 0.2) * mm});
            skLineSegment(sketch, "E342", {"start": v(12.86, 0.2) * mm, "end": v(12.86, 0.4) * mm});
            skLineSegment(sketch, "E343", {"start": v(12.86, 0.4) * mm, "end": v(12.84, 0.54) * mm});
            skLineSegment(sketch, "E344", {"start": v(12.84, 0.54) * mm, "end": v(12.82, 0.63) * mm});
            skLineSegment(sketch, "E345", {"start": v(12.82, 0.63) * mm, "end": v(12.8, 0.7) * mm});
            skLineSegment(sketch, "E346", {"start": v(12.8, 0.7) * mm, "end": v(12.76, 0.77) * mm});
            skLineSegment(sketch, "E347", {"start": v(12.76, 0.77) * mm, "end": v(12.6, 0.96) * mm});
            skLineSegment(sketch, "E348", {"start": v(12.6, 0.96) * mm, "end": v(12.4, 1.08) * mm});
            skLineSegment(sketch, "E349", {"start": v(12.4, 1.08) * mm, "end": v(12.15, 1.1) * mm});
            skLineSegment(sketch, "E350", {"start": v(12.15, 1.1) * mm, "end": v(11.9, 1.04) * mm});
            skLineSegment(sketch, "E351", {"start": v(11.9, 1.04) * mm, "end": v(11.7, 0.9) * mm});
            skLineSegment(sketch, "E352", {"start": v(11.7, 0.9) * mm, "end": v(11.57, 0.72) * mm});
            skLineSegment(sketch, "E353", {"start": v(11.57, 0.72) * mm, "end": v(11.54, 0.65) * mm});
            skLineSegment(sketch, "E354", {"start": v(11.54, 0.65) * mm, "end": v(11.52, 0.58) * mm});
            skLineSegment(sketch, "E355", {"start": v(11.52, 0.58) * mm, "end": v(11.5, 0.48) * mm});
            skLineSegment(sketch, "E356", {"start": v(11.5, 0.48) * mm, "end": v(11.5, 0.34) * mm});
            skLineSegment(sketch, "E357", {"start": v(11.5, 0.34) * mm, "end": v(11.49, 0.14) * mm});
            skLineSegment(sketch, "E358", {"start": v(11.49, 0.14) * mm, "end": v(11.48, -0.13) * mm});
            skLineSegment(sketch, "E359", {"start": v(11.48, -0.13) * mm, "end": v(11.48, -0.5) * mm});
            skLineSegment(sketch, "E360", {"start": v(11.48, -0.5) * mm, "end": v(11.48, -0.99) * mm});
            skLineSegment(sketch, "E361", {"start": v(11.48, -0.99) * mm, "end": v(11.48, -2.35) * mm});
            skLineSegment(sketch, "E362", {"start": v(11.48, -2.35) * mm, "end": v(9.75, -2.35) * mm});
            skLineSegment(sketch, "E363", {"start": v(9.75, -2.35) * mm, "end": v(9.75, 0.1) * mm});
            skLineSegment(sketch, "E364", {"start": v(9.75, 0.1) * mm, "end": v(9.75, 0.1) * mm});
            skLineSegment(sketch, "E365", {"start": v(15.44, -0.57) * mm, "end": v(15.44, 1.18) * mm});
            skLineSegment(sketch, "E366", {"start": v(15.44, 1.18) * mm, "end": v(14.85, 1.18) * mm});
            skLineSegment(sketch, "E367", {"start": v(14.85, 1.18) * mm, "end": v(14.85, 2.57) * mm});
            skLineSegment(sketch, "E368", {"start": v(14.85, 2.57) * mm, "end": v(15.44, 2.57) * mm});
            skLineSegment(sketch, "E369", {"start": v(15.44, 2.57) * mm, "end": v(15.44, 3.8) * mm});
            skLineSegment(sketch, "E370", {"start": v(15.44, 3.8) * mm, "end": v(17.17, 3.8) * mm});
            skLineSegment(sketch, "E371", {"start": v(17.17, 3.8) * mm, "end": v(17.17, 2.57) * mm});
            skLineSegment(sketch, "E372", {"start": v(17.17, 2.57) * mm, "end": v(18.3, 2.57) * mm});
            skLineSegment(sketch, "E373", {"start": v(18.3, 2.57) * mm, "end": v(18.3, 1.18) * mm});
            skLineSegment(sketch, "E374", {"start": v(18.3, 1.18) * mm, "end": v(17.17, 1.18) * mm});
            skLineSegment(sketch, "E375", {"start": v(17.17, 1.18) * mm, "end": v(17.17, -2.32) * mm});
            skLineSegment(sketch, "E376", {"start": v(17.17, -2.32) * mm, "end": v(15.44, -2.32) * mm});
            skLineSegment(sketch, "E377", {"start": v(15.44, -2.32) * mm, "end": v(15.44, -0.57) * mm});
            skLineSegment(sketch, "E378", {"start": v(18.67, -2.33) * mm, "end": v(18.4, -2.2) * mm});
            skLineSegment(sketch, "E379", {"start": v(18.4, -2.2) * mm, "end": v(18.17, -2.02) * mm});
            skLineSegment(sketch, "E380", {"start": v(18.17, -2.02) * mm, "end": v(18, -1.79) * mm});
            skLineSegment(sketch, "E381", {"start": v(18, -1.79) * mm, "end": v(17.9, -1.51) * mm});
            skLineSegment(sketch, "E382", {"start": v(17.9, -1.51) * mm, "end": v(17.9, -1.38) * mm});
            skLineSegment(sketch, "E383", {"start": v(17.9, -1.38) * mm, "end": v(17.9, -1.22) * mm});
            skLineSegment(sketch, "E384", {"start": v(17.9, -1.22) * mm, "end": v(17.91, -1.07) * mm});
            skLineSegment(sketch, "E385", {"start": v(17.91, -1.07) * mm, "end": v(17.95, -0.95) * mm});
            skLineSegment(sketch, "E386", {"start": v(17.95, -0.95) * mm, "end": v(18.06, -0.73) * mm});
            skLineSegment(sketch, "E387", {"start": v(18.06, -0.73) * mm, "end": v(18.21, -0.54) * mm});
            skLineSegment(sketch, "E388", {"start": v(18.21, -0.54) * mm, "end": v(18.4, -0.4) * mm});
            skLineSegment(sketch, "E389", {"start": v(18.4, -0.4) * mm, "end": v(18.65, -0.29) * mm});
            skLineSegment(sketch, "E390", {"start": v(18.65, -0.29) * mm, "end": v(18.78, -0.26) * mm});
            skLineSegment(sketch, "E391", {"start": v(18.78, -0.26) * mm, "end": v(18.95, -0.25) * mm});
            skLineSegment(sketch, "E392", {"start": v(18.95, -0.25) * mm, "end": v(19.11, -0.26) * mm});
            skLineSegment(sketch, "E393", {"start": v(19.11, -0.26) * mm, "end": v(19.24, -0.29) * mm});
            skLineSegment(sketch, "E394", {"start": v(19.24, -0.29) * mm, "end": v(19.56, -0.45) * mm});
            skLineSegment(sketch, "E395", {"start": v(19.56, -0.45) * mm, "end": v(19.8, -0.68) * mm});
            skLineSegment(sketch, "E396", {"start": v(19.8, -0.68) * mm, "end": v(19.95, -0.97) * mm});
            skLineSegment(sketch, "E397", {"start": v(19.95, -0.97) * mm, "end": v(20, -1.3) * mm});
            skLineSegment(sketch, "E398", {"start": v(20, -1.3) * mm, "end": v(19.94, -1.65) * mm});
            skLineSegment(sketch, "E399", {"start": v(19.94, -1.65) * mm, "end": v(19.78, -1.95) * mm});
            skLineSegment(sketch, "E400", {"start": v(19.78, -1.95) * mm, "end": v(19.53, -2.19) * mm});
            skLineSegment(sketch, "E401", {"start": v(19.53, -2.19) * mm, "end": v(19.22, -2.33) * mm});
            skLineSegment(sketch, "E402", {"start": v(19.22, -2.33) * mm, "end": v(19.1, -2.35) * mm});
            skLineSegment(sketch, "E403", {"start": v(19.1, -2.35) * mm, "end": v(18.94, -2.35) * mm});
            skLineSegment(sketch, "E404", {"start": v(18.94, -2.35) * mm, "end": v(18.79, -2.35) * mm});
            skLineSegment(sketch, "E405", {"start": v(18.79, -2.35) * mm, "end": v(18.67, -2.33) * mm});
            skLineSegment(sketch, "E406", {"start": v(18.67, -2.33) * mm, "end": v(18.67, -2.33) * mm});
            skSolve(sketch);
        }
        {
            var Q0;
            Q0 = qSketchRegion(id + "F0", true);
            extrude(context, id + "F2", {"entities" : qUnion([Q0]), "oppositeDirection" : true, "depth" : 3 * mm});
        }
        {
            var Q0;
            Q0=makeQuery(id+"F2.opExtrude","SWEPT_EDGE",EDGE,{"disambiguationData":[OSD([sQuery(id+"F0.wireOp",EDGE,"E0.top"),sQuery(id+"F0.wireOp",EDGE,"E0.right")])]});
            var Q1;
            Q1=makeQuery(id+"F2.opExtrude","SWEPT_EDGE",EDGE,{"disambiguationData":[OSD([sQuery(id+"F0.wireOp",EDGE,"E0.bottom"),sQuery(id+"F0.wireOp",EDGE,"E0.right")])]});
            var Q2;
            Q2=makeQuery(id+"F2.opExtrude","SWEPT_EDGE",EDGE,{"disambiguationData":[OSD([sQuery(id+"F0.wireOp",EDGE,"E0.bottom"),sQuery(id+"F0.wireOp",EDGE,"E0.left")])]});
            var Q3;
            Q3=makeQuery(id+"F2.opExtrude","SWEPT_EDGE",EDGE,{"disambiguationData":[OSD([sQuery(id+"F0.wireOp",EDGE,"E0.top"),sQuery(id+"F0.wireOp",EDGE,"E0.left")])]});
            fillet(context, id + "F3", {"entities" : qUnion([Q0, Q1, Q2, Q3]), "radius" : 5 * mm, "tangentPropagation" : true, "allowEdgeOverflow" : false});
        }
        {
            var Q0;
            Q0=makeQuery(id+"F2.opExtrude","CAP_EDGE",EDGE,{"disambiguationData":[OSD([sQuery(id+"F0.wireOp",EDGE,"E0.bottom")])],"isStart":true});
            var Q1;
            Q1=makeQuery(id+"F2.opExtrude","CAP_EDGE",EDGE,{"disambiguationData":[OSD([sQuery(id+"F0.wireOp",EDGE,"E0.right")])],"isStart":false});
            fillet(context, id + "F4", {"entities" : qUnion([Q0, Q1]), "radius" : 1 * mm, "tangentPropagation" : true, "allowEdgeOverflow" : false});
        }
        {
            var Q0;
            Q0 = qSketchRegion(id + "F1", true);
            extrude(context, id + "F5", {"entities" : qUnion([Q0]), "operationType" : NewBodyOperationType.REMOVE, "oppositeDirection" : true, "depth" : 0.5 * mm});
        }
        {
            var Q0;
            Q0=makeQuery(id+"F0.imprint","IMPRINT",FACE,{"disambiguationData":[TD([[makeQuery(id+"F0.imprint","IMPRINT",EDGE,{"derivedFrom":sQuery(id+"F0.wireOp",EDGE,"E0.bottom")}),-1.0]])]});
            var sketch = newSketch(context, id + "F6", { "sketchPlane" : qUnion([Q0])});
            skCircle(sketch, "E407", {"center": v(-21, 6) * mm, "radius": 1.5 * mm});
            skSolve(sketch);
        }
        {
            var Q0;
            Q0 = qSketchRegion(id + "F6", true);
            extrude(context, id + "F7", {"entities" : qUnion([Q0]), "operationType" : NewBodyOperationType.REMOVE, "endBound" : BoundingType.THROUGH_ALL, "oppositeDirection" : true, "depth" : 25 * mm});
        }
        {
            var Q0;
            Q0=makeQuery(id+"F7.boolean.opBoolean","COPY",EDGE,{"derivedFrom":makeQuery(id+"F7.opExtrude","CAP_EDGE",EDGE,{"disambiguationData":[OSD([sQuery(id+"F6.wireOp",EDGE,"E407")])],"isStart":true})});
            var Q1;
            Q1=makeQuery(id+"F7.boolean.opBoolean","INTERSECT",EDGE,{"derivedFrom":[makeQuery(id+"F2.opExtrude","CAP_FACE",FACE,{"disambiguationData":[OSD([sQuery(id+"F0.wireOp",EDGE,"E0.bottom"),sQuery(id+"F0.wireOp",EDGE,"E0.top"),sQuery(id+"F0.wireOp",EDGE,"E0.left"),sQuery(id+"F0.wireOp",EDGE,"E0.right")])],"isStart":false}),makeQuery(id+"F7.opExtrude","SWEPT_FACE",FACE,{"disambiguationData":[OSD([sQuery(id+"F6.wireOp",EDGE,"E407")])]})]});
            fillet(context, id + "F8", {"entities" : qUnion([Q0, Q1]), "radius" : 0.4 * mm, "tangentPropagation" : true, "allowEdgeOverflow" : false});
        }
    });
